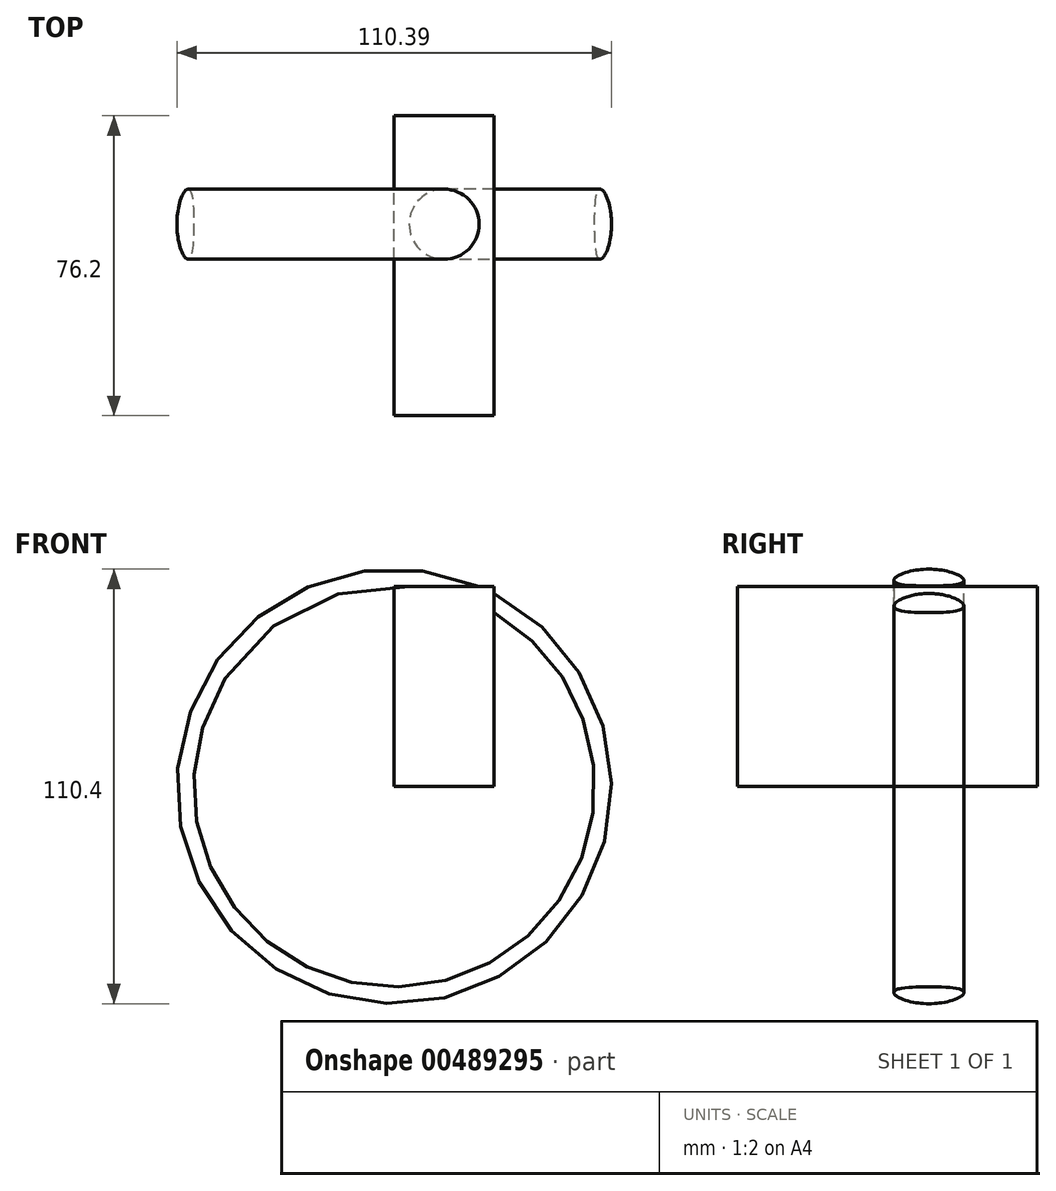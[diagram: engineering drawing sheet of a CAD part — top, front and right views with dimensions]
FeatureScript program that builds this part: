
annotation { "Feature Type Name" : "Feature", "Feature Type Description" : "" }
export const myFeature = defineFeature(function(context is Context, id is Id, definition is map)
    precondition{}
    {
        {
            var Q0;
            Q0=qCreatedBy(makeId("Front.planeOp"),FACE);
            var sketch = newSketch(context, id + "F0", { "sketchPlane" : qUnion([Q0])});
            skLineSegment(sketch, "E0.bottom", {"start": v(-88.1, -5.55) * mm, "end": v(-113.5, -5.55) * mm});
            skLineSegment(sketch, "E0.top", {"start": v(-88.1, -56.35) * mm, "end": v(-113.5, -56.35) * mm});
            skLineSegment(sketch, "E0.left", {"start": v(-88.1, -5.55) * mm, "end": v(-88.1, -56.35) * mm});
            skLineSegment(sketch, "E0.right", {"start": v(-113.5, -5.55) * mm, "end": v(-113.5, -56.35) * mm});
            skPoint(sketch, "E0.middle", {"position": v(-100.8, -30.95) * mm});
            skSolve(sketch);
        }
        {
            var Q0;
            Q0=makeQuery(id+"F0.imprint","IMPRINT",FACE,{"disambiguationData":[TD([[makeQuery(id+"F0.imprint","IMPRINT",EDGE,{"derivedFrom":sQuery(id+"F0.wireOp",EDGE,"E0.bottom")}),1.0]])]});
            extrude(context, id + "F1", {"entities" : qUnion([Q0]), "depth" : 76.2 * mm});
        }
        {
            var Q0;
            Q0=makeQuery(id+"F1.opExtrude","SWEPT_FACE",FACE,{"disambiguationData":[OSD([sQuery(id+"F0.wireOp",EDGE,"E0.bottom")])]});
            var sketch = newSketch(context, id + "F2", { "sketchPlane" : qUnion([Q0])});
            skCircle(sketch, "E1", {"center": v(-100.8, -27.55) * mm, "radius": 8.89 * mm});
            skSolve(sketch);
        }
        {
            var Q0;
            Q0=makeQuery(id+"F2.imprint","IMPRINT",FACE,{"disambiguationData":[TD([[makeQuery(id+"F2.imprint","IMPRINT",EDGE,{"derivedFrom":sQuery(id+"F2.wireOp",EDGE,"E1")}),1.0]])]});
            var Q1;
            Q1=makeQuery(id+"F1.opExtrude","SWEPT_EDGE",EDGE,{"disambiguationData":[OSD([sQuery(id+"F0.wireOp",EDGE,"E0.top"),sQuery(id+"F0.wireOp",EDGE,"E0.right")])]});
            revolve(context, id + "F3", {"operationType" : NewBodyOperationType.ADD, "entities" : qUnion([Q0]), "axis" : qUnion([Q1]), "revolveType" : RevolveType.FULL, "oppositeDirection" : true});
        }
    });
